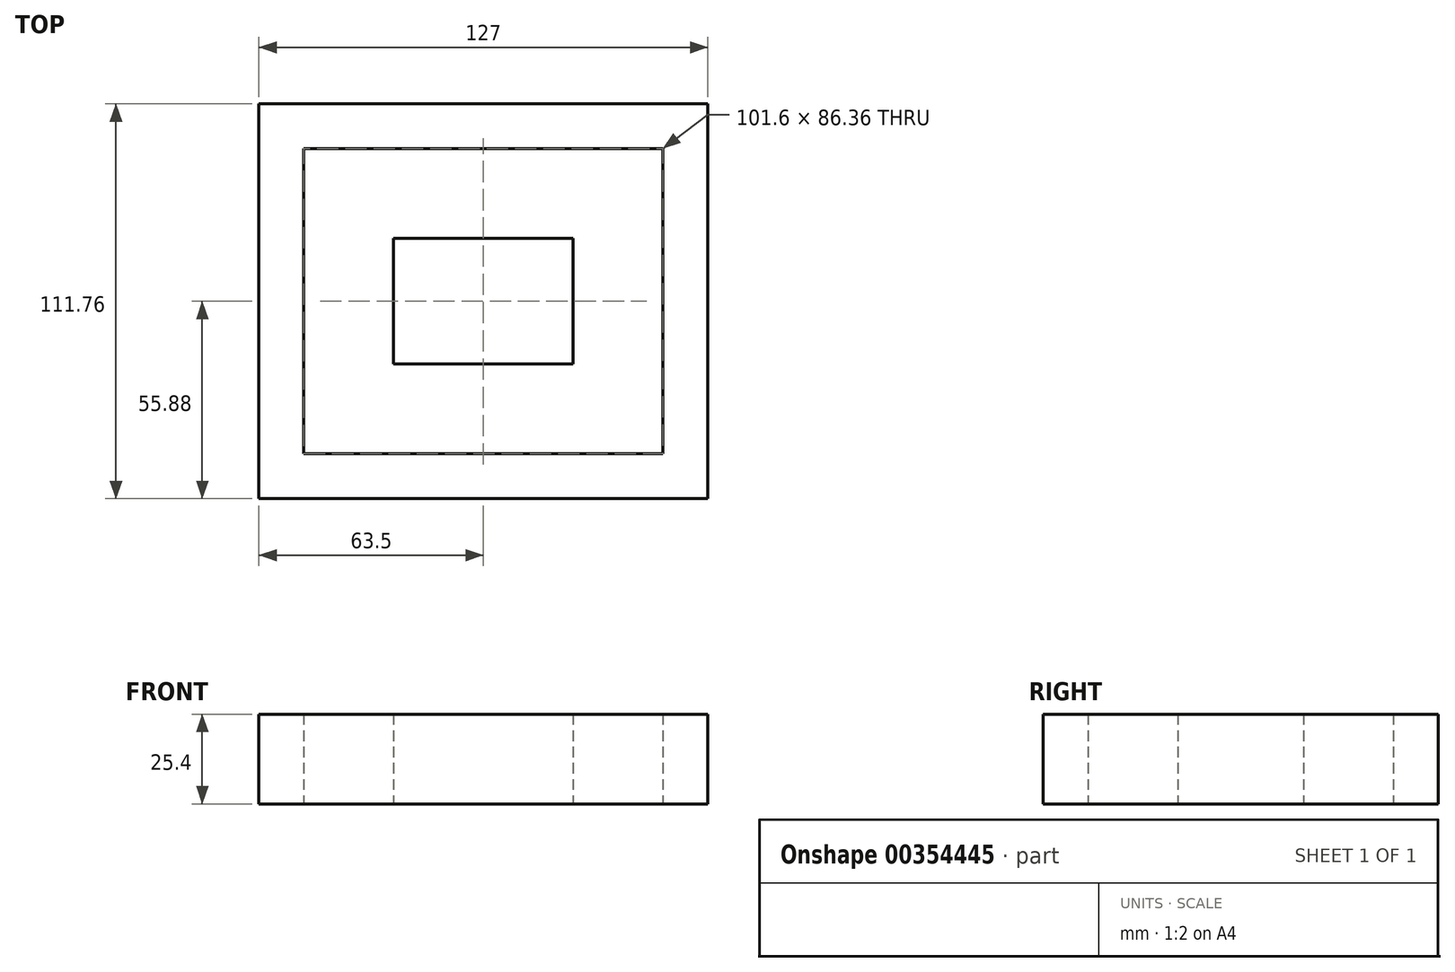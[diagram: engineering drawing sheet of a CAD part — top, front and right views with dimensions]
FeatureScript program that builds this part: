
annotation { "Feature Type Name" : "Feature", "Feature Type Description" : "" }
export const myFeature = defineFeature(function(context is Context, id is Id, definition is map)
    precondition{}
    {
        {
            var Q0;
            Q0=qCreatedBy(makeId("Top.planeOp"),FACE);
            var sketch = newSketch(context, id + "F0", { "sketchPlane" : qUnion([Q0])});
            skLineSegment(sketch, "E0.bottom", {"start": v(63.5, 55.88) * mm, "end": v(-63.5, 55.88) * mm});
            skLineSegment(sketch, "E0.top", {"start": v(63.5, -55.88) * mm, "end": v(-63.5, -55.88) * mm});
            skLineSegment(sketch, "E0.left", {"start": v(63.5, 55.88) * mm, "end": v(63.5, -55.88) * mm});
            skLineSegment(sketch, "E0.right", {"start": v(-63.5, 55.88) * mm, "end": v(-63.5, -55.88) * mm});
            skPoint(sketch, "E0.middle", {"position": v(0, 0) * mm});
            skLineSegment(sketch, "E1.bottom", {"start": v(50.8, 43.18) * mm, "end": v(-50.8, 43.18) * mm});
            skLineSegment(sketch, "E1.top", {"start": v(50.8, -43.18) * mm, "end": v(-50.8, -43.18) * mm});
            skLineSegment(sketch, "E1.left", {"start": v(50.8, 43.18) * mm, "end": v(50.8, -43.18) * mm});
            skLineSegment(sketch, "E1.right", {"start": v(-50.8, 43.18) * mm, "end": v(-50.8, -43.18) * mm});
            skLineSegment(sketch, "E2.bottom", {"start": v(38.1, 30.48) * mm, "end": v(-38.1, 30.48) * mm});
            skLineSegment(sketch, "E2.top", {"start": v(38.1, -30.48) * mm, "end": v(-38.1, -30.48) * mm});
            skLineSegment(sketch, "E2.left", {"start": v(38.1, 30.48) * mm, "end": v(38.1, -30.48) * mm});
            skLineSegment(sketch, "E2.right", {"start": v(-38.1, 30.48) * mm, "end": v(-38.1, -30.48) * mm});
            skLineSegment(sketch, "E3.bottom", {"start": v(25.4, 17.78) * mm, "end": v(-25.4, 17.78) * mm});
            skLineSegment(sketch, "E3.top", {"start": v(25.4, -17.78) * mm, "end": v(-25.4, -17.78) * mm});
            skLineSegment(sketch, "E3.left", {"start": v(25.4, 17.78) * mm, "end": v(25.4, -17.78) * mm});
            skLineSegment(sketch, "E3.right", {"start": v(-25.4, 17.78) * mm, "end": v(-25.4, -17.78) * mm});
            skSolve(sketch);
        }
        {
            var Q0;
            Q0=makeQuery(id+"F0.imprint","IMPRINT",FACE,{"disambiguationData":[TD([[makeQuery(id+"F0.imprint","IMPRINT",EDGE,{"derivedFrom":sQuery(id+"F0.wireOp",EDGE,"E3.bottom")}),1.0]])]});
            var Q1;
            Q1 = qSketchRegion(id + "F0", true);
            extrude(context, id + "F1", {"entities" : qUnion([Q0, Q1]), "depth" : 25.4 * mm});
        }
    });
